# Revit family: QF_Friginox_MX 29S-2 TS7_MX 29SX-2 TS7_SXP 29cS-2 TS7-AC
name_source: partatom
category: Specialty Equipment
units: mm (PartAtom-declared; Revit-internal decimal feet)

## family parameters
Always vertical = Yes
Cut with Voids When Loaded = No
Part Type = Normal
Room Calculation Point = No
Round Connector Dimension = Use Diameter
Shared = No
Work Plane-Based = No

## types (6) — shared parameters
Accessory = No
CE Approved = Yes
Chilled Water Return Size = 0 mm
Chilled Water Supply Flow = 0.0 L/s
Chilled Water Supply Size = 0 mm
Condensate Return Connection Height = 105 mm  [stored 0.344488 ft]
Condensate Return Size = 32 mm
Conn Plug = Only cable
Cycle = 50 Hz
D15 = 15 mm  [stored 0.0492126 ft]
Depth Actual = 1295 mm
Direct Waste Size = 20 mm
Direct Waste_Note = Direct Waste
Door_Depth = 135 mm  [stored 0.442913 ft]
Door_W = 900 mm  [stored 2.95276 ft]
Elec Connection Height = 2025 mm  [stored 6.6437 ft]
Electric power = 4400 W
FL Amps = 0 A
Foodservice Equipment Identifier = Yes
Groupe frigorifique = A distance uniq.
Height Actual = 2170 mm  [stored 7.11942 ft]
Identify Quantity as Lot = No
Keynote = 0
Length Actual = 1460 mm  [stored 4.79003 ft]
Main switch integrated = No
Manufacturer = FRIGINOX
Mat_Case = QF_Stainless-Brushed
Mat_Clearance = QF_Clearance
Mat_Legs = QF_Stainless-Brushed
Number of Poles = 3
Phase = 3
Potential Equalisation = Yes
Refrigerant Compressor Remote = Yes
Refrigerant Volume = 0.0 L/s
Refrigeration Defrost Drain = Yes
Refrigeration Liquid Line Size = 15 mm
Refrigeration Suction Line Size = 28 mm
URL Cutsheet = FTEC_MX29S-2TS7_MX29SX-2TS7_SXP29CS-2TS7_FR_0922.pdf
URL Manufacturer = http://www.friginox.com
Volt Free Conn = No
Volts = 400 V
Weight = 360.00 kg
zero-valued in all types: Chilled Water Return Connection Height, Chilled Water Supply Connection Height, Cost, Default Elevation, Direct Waste Connection Height, Refrigerant Mass

## per-type parameters (varying)
| type | Description | Item Number | LH | Model | RH |
| MX 29S-2 TS7_RH | Blast Chiller, Roll-in 1 trolley GN2/1, 160kg, 110min | FX39272643 | No | MX 29S-2 TS7 | Yes |
| MX 29S-2 TS7_LH | Blast Chiller, Roll-in 1 trolley GN2/1, 160kg, 110min | FX39272643 | Yes | MX 29S-2 TS7 | No |
| MX 29SX-2 TS7_RH | Blast Chiller, Roll-in 1 trolley GN2/1, 160kg, 85min | FX39272644 | No | MX 29SX-2 TS7 | Yes |
| MX 29SX-2 TS7_LH | Blast Chiller, Roll-in 1 trolley GN2/1, 160kg, 85min | FX39272644 | Yes | MX 29SX-2 TS7 | No |
| SXP 29cS-2 TS7_RH | Blast Freezer, Roll-in 1 trolley 600x800, 60kg | FX39272679 | No | SXP 29cS-2 TS7 | Yes |
| SXP 29cS-2 TS7_LH | Blast Freezer, Roll-in 1 trolley 600x800, 60kg | FX39272679 | Yes | SXP 29cS-2 TS7 | No |

note: [stored X ft] marks values corroborated as IEEE doubles in the binary element streams (Revit-internal decimal feet)

## geometry (parser evidence)
native form markers: Sweep x11
no freeform markers — native parametric forms only
